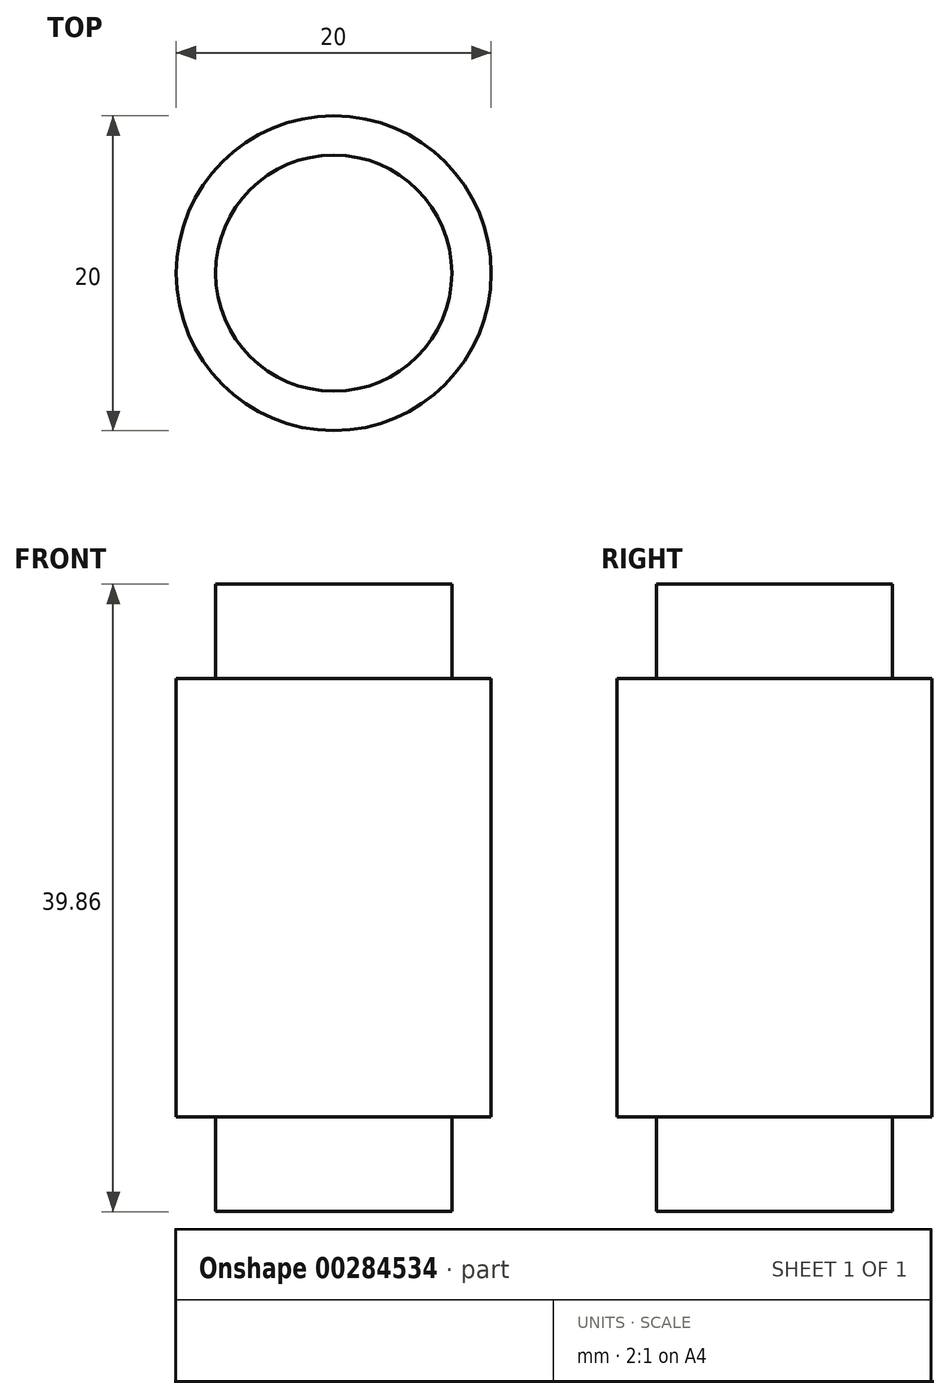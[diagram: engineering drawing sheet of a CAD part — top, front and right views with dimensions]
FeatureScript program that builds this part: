
annotation { "Feature Type Name" : "Feature", "Feature Type Description" : "" }
export const myFeature = defineFeature(function(context is Context, id is Id, definition is map)
    precondition{}
    {
        {
            var Q0;
            Q0=qCreatedBy(makeId("Top.planeOp"),FACE);
            var sketch = newSketch(context, id + "F0", { "sketchPlane" : qUnion([Q0])});
            skCircle(sketch, "E0", {"center": v(-54.49, -46.73) * mm, "radius": 10 * mm});
            skSolve(sketch);
        }
        {
            var Q0;
            Q0=qSketchRegion(id+"F0",true);
            extrude(context, id + "F1", {"entities" : qUnion([Q0]), "endBound" : BoundingType.SYMMETRIC, "depth" : 27.85 * mm});
        }
        {
            var Q0;
            Q0=makeQuery(id+"F1.opExtrude","CAP_FACE",FACE,{"disambiguationData":[OSD([sQuery(id+"F0.wireOp",EDGE,"E0")])],"isStart":false});
            var sketch = newSketch(context, id + "F2", { "sketchPlane" : qUnion([Q0])});
            skCircle(sketch, "E1", {"center": v(-54.49, -46.73) * mm, "radius": 7.5 * mm});
            skSolve(sketch);
        }
        {
            var Q0;
            Q0=qSketchRegion(id+"F2",true);
            extrude(context, id + "F3", {"entities" : qUnion([Q0]), "depth" : 6 * mm});
        }
        {
            var Q0;
            Q0=makeQuery(id+"F3.opExtrude","SWEPT_BODY",BODY,{"disambiguationData":[OSD([sQuery(id+"F2.wireOp",EDGE,"E1")])]});
            var Q1;
            Q1=qCreatedBy(makeId("Top.planeOp"),FACE);
            mirror(context, id + "F4", {"operationType" : NewBodyOperationType.ADD, "entities" : qUnion([Q0]), "mirrorPlane" : qUnion([Q1])});
        }
    });
